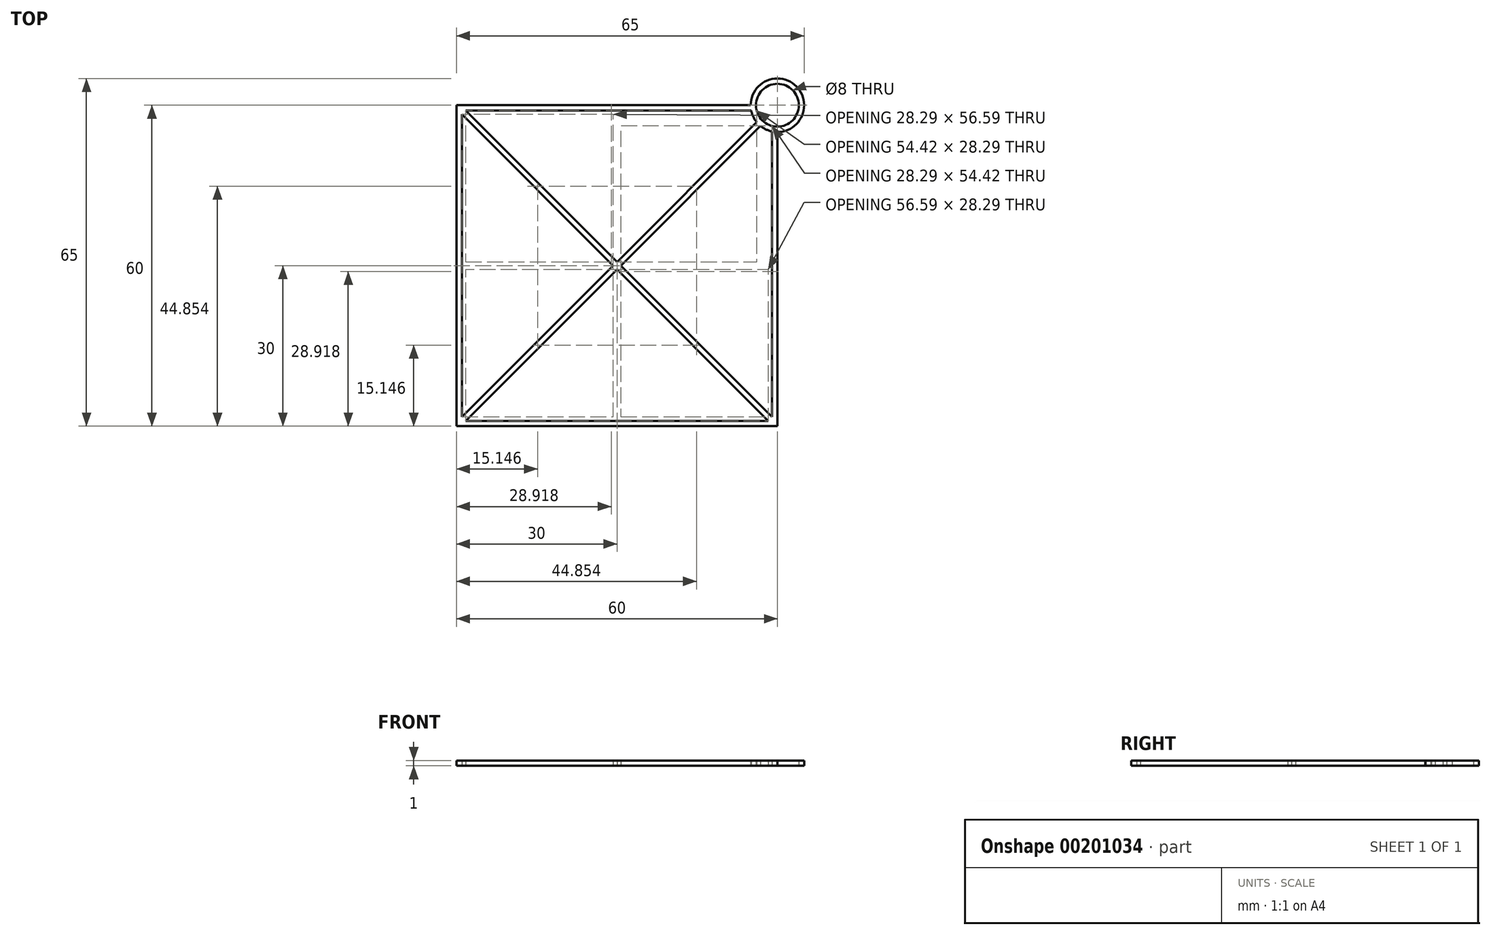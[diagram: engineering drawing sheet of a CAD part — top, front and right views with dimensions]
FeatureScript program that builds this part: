
annotation { "Feature Type Name" : "Feature", "Feature Type Description" : "" }
export const myFeature = defineFeature(function(context is Context, id is Id, definition is map)
    precondition{}
    {
        {
            var Q0;
            Q0=qCreatedBy(makeId("Top.planeOp"),FACE);
            var sketch = newSketch(context, id + "F0", { "sketchPlane" : qUnion([Q0])});
            skLineSegment(sketch, "E0.bottom", {"start": v(-30, 30) * mm, "end": v(25, 30) * mm});
            skLineSegment(sketch, "E0.top", {"start": v(-30, -30) * mm, "end": v(30, -30) * mm});
            skLineSegment(sketch, "E0.left", {"start": v(-30, 30) * mm, "end": v(-30, -30) * mm});
            skLineSegment(sketch, "E0.right", {"start": v(30, 25) * mm, "end": v(30, -30) * mm});
            skPoint(sketch, "E1", {"position": v(0, 30) * mm});
            skPoint(sketch, "E2", {"position": v(-30, 0) * mm});
            skArc(sketch, "E3", {"start": v(26.84, 26.13) * mm, "mid": v(27.86, 25.48) * mm, "end": v(29, 25.1) * mm});
            skLineSegment(sketch, "E4.0", {"start": v(-28.3, 29) * mm, "end": v(25.1, 29) * mm});
            skLineSegment(sketch, "E4.1", {"start": v(-29, 28.3) * mm, "end": v(-29, -28.3) * mm});
            skLineSegment(sketch, "E4.2", {"start": v(-28.3, -29) * mm, "end": v(28.3, -29) * mm});
            skLineSegment(sketch, "E4.3", {"start": v(29, 25.1) * mm, "end": v(29, -28.3) * mm});
            skLineSegment(sketch, "E5.0", {"start": v(-28.3, 29) * mm, "end": v(0, 0.7) * mm});
            skLineSegment(sketch, "E6.0", {"start": v(-28.3, -29) * mm, "end": v(0, -0.7) * mm});
            skLineSegment(sketch, "E7.MirrorCS", {"start": v(-29, -28.3) * mm, "end": v(-0.7, 0) * mm});
            skLineSegment(sketch, "E8.MirrorCS", {"start": v(-29, 28.3) * mm, "end": v(-0.7, 0) * mm});
            skCircle(sketch, "E9.0", {"center": v(30, 30) * mm, "radius": 4 * mm});
            skArc(sketch, "E10.trimOffspring", {"start": v(30, 25) * mm, "mid": v(33.54, 33.54) * mm, "end": v(25, 30) * mm});
            skArc(sketch, "E11.trimOffspring", {"start": v(25.1, 29) * mm, "mid": v(25.48, 27.86) * mm, "end": v(26.13, 26.84) * mm});
            skLineSegment(sketch, "E12.trimOffspring", {"start": v(0.7, 0) * mm, "end": v(29, -28.3) * mm});
            skLineSegment(sketch, "E13.trimOffspring", {"start": v(0, 0.7) * mm, "end": v(26.13, 26.84) * mm});
            skLineSegment(sketch, "E14.trimOffspring", {"start": v(0, -0.7) * mm, "end": v(28.3, -29) * mm});
            skLineSegment(sketch, "E15.trimOffspring", {"start": v(0.7, 0) * mm, "end": v(26.84, 26.13) * mm});
            skSolve(sketch);
        }
        {
            var Q0;
            Q0=makeQuery(id+"F0.imprint","IMPRINT",FACE,{"disambiguationData":[TD([[makeQuery(id+"F0.imprint","IMPRINT",EDGE,{"derivedFrom":sQuery(id+"F0.wireOp",EDGE,"E0.bottom")}),-1.0]])]});
            extrude(context, id + "F1", {"entities" : qUnion([Q0]), "depth" : 1 * mm});
        }
    });
